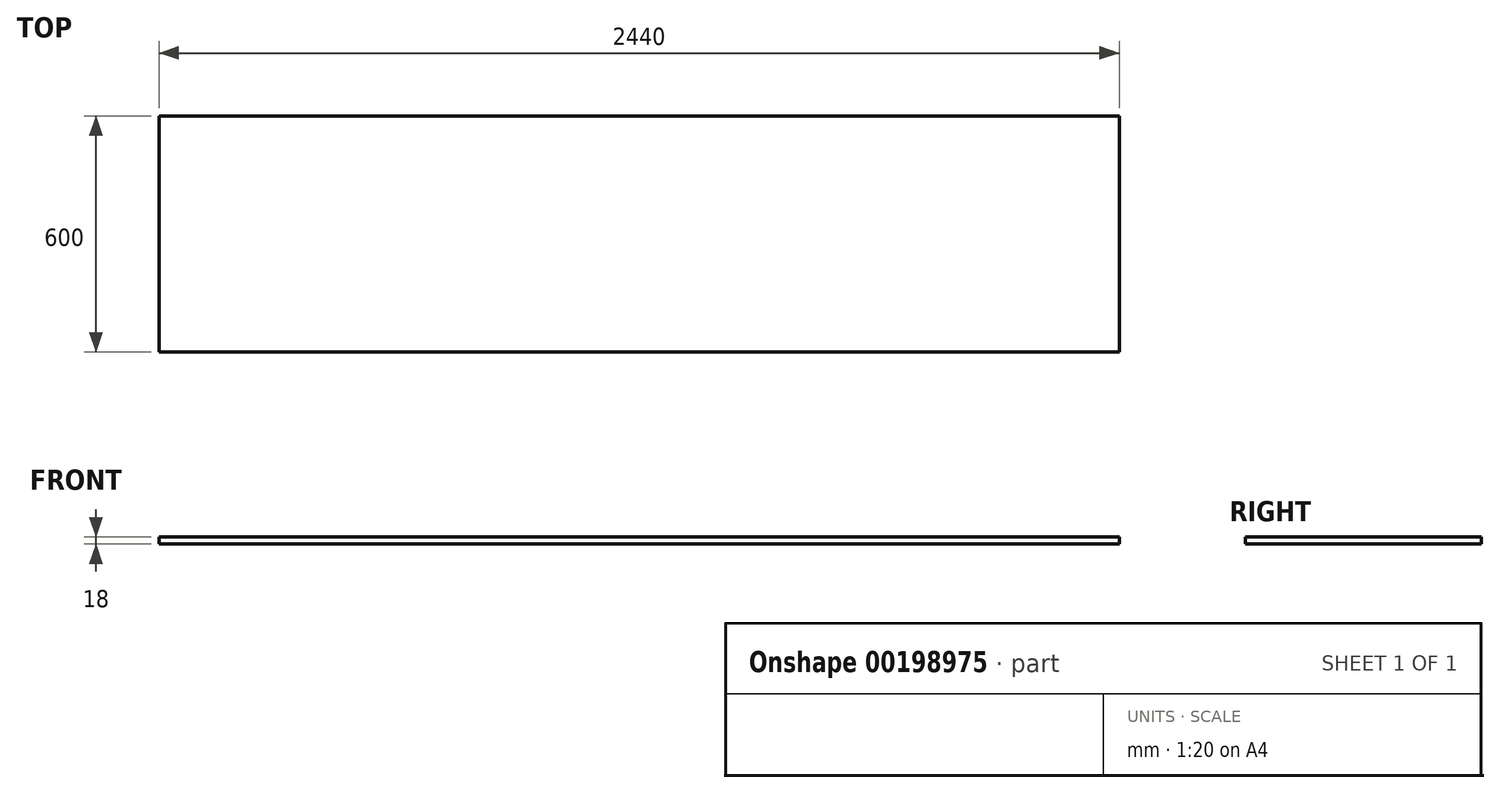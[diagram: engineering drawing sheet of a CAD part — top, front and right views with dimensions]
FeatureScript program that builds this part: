
annotation { "Feature Type Name" : "Feature", "Feature Type Description" : "" }
export const myFeature = defineFeature(function(context is Context, id is Id, definition is map)
    precondition{}
    {
        {
            var Q0;
            Q0=qCreatedBy(makeId("Top.planeOp"),FACE);
            var sketch = newSketch(context, id + "F0", { "sketchPlane" : qUnion([Q0])});
            skLineSegment(sketch, "E0.bottom", {"start": v(-1301.4, 426.93) * mm, "end": v(1138.6, 426.93) * mm});
            skLineSegment(sketch, "E0.top", {"start": v(-1301.4, -173.07) * mm, "end": v(1138.6, -173.07) * mm});
            skLineSegment(sketch, "E0.left", {"start": v(-1301.4, 426.93) * mm, "end": v(-1301.4, -173.07) * mm});
            skLineSegment(sketch, "E0.right", {"start": v(1138.6, 426.93) * mm, "end": v(1138.6, -173.07) * mm});
            skSolve(sketch);
        }
        {
            var Q0;
            Q0=makeQuery(id+"F0.imprint","IMPRINT",FACE,{"disambiguationData":[TD([[makeQuery(id+"F0.imprint","IMPRINT",EDGE,{"derivedFrom":sQuery(id+"F0.wireOp",EDGE,"E0.bottom")}),-1.0]])]});
            extrude(context, id + "F1", {"entities" : qUnion([Q0]), "depth" : 18 * mm});
        }
    });
